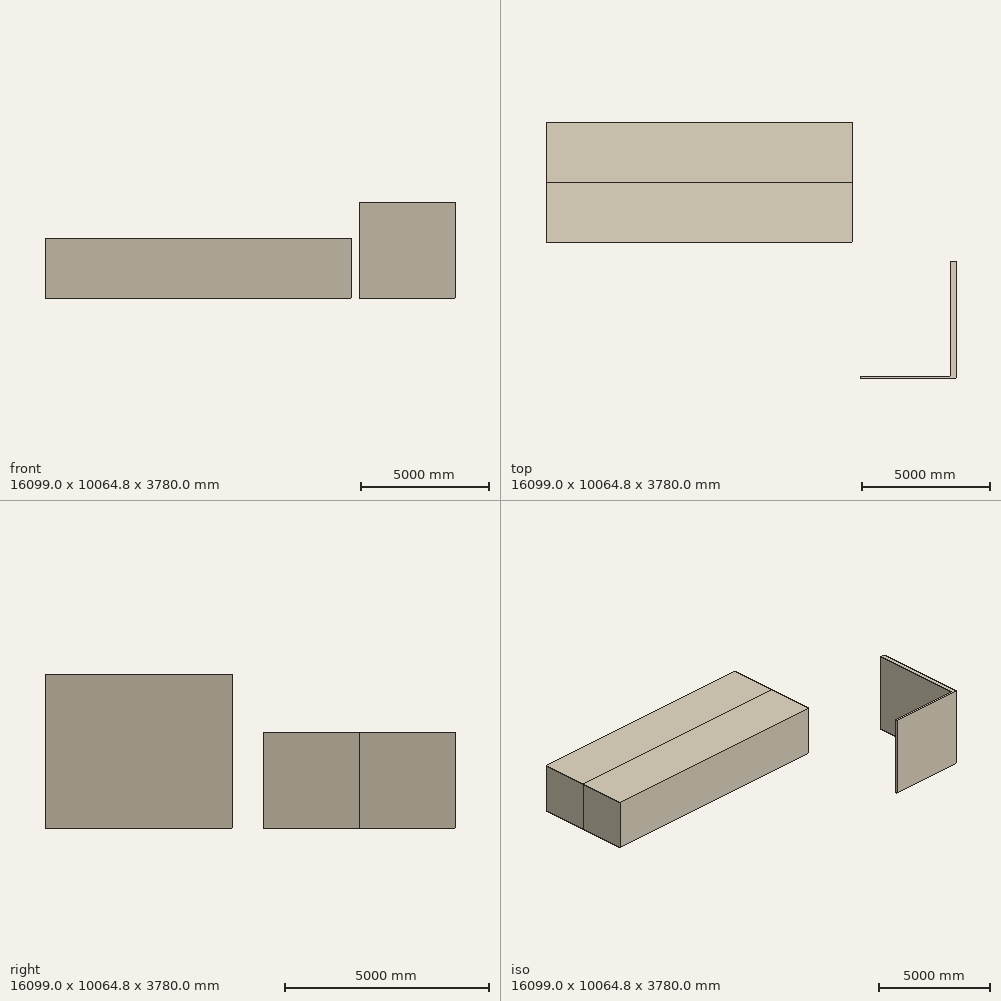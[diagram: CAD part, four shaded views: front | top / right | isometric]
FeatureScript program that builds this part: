
annotation { "Feature Type Name" : "Feature", "Feature Type Description" : "" }
export const myFeature = defineFeature(function(context is Context, id is Id, definition is map)
    precondition{}
    {
        {
            var Q0;
            Q0=qCreatedBy(makeId("Top.planeOp"),FACE);
            var sketch = newSketch(context, id + "F0", { "sketchPlane" : qUnion([Q0])});
            skLineSegment(sketch, "E0.bottom", {"start": v(0, 0) * mm, "end": v(12029, 0) * mm});
            skLineSegment(sketch, "E0.top", {"start": v(0, 2346) * mm, "end": v(12029, 2346) * mm});
            skLineSegment(sketch, "E0.left", {"start": v(0, 0) * mm, "end": v(0, 2346) * mm});
            skLineSegment(sketch, "E0.right", {"start": v(12029, 0) * mm, "end": v(12029, 2346) * mm});
            skLineSegment(sketch, "E1.bottom", {"start": v(0, 2356) * mm, "end": v(12029, 2356) * mm});
            skLineSegment(sketch, "E1.top", {"start": v(0, 4702) * mm, "end": v(12029, 4702) * mm});
            skLineSegment(sketch, "E1.left", {"start": v(0, 2356) * mm, "end": v(0, 4702) * mm});
            skLineSegment(sketch, "E1.right", {"start": v(12029, 2356) * mm, "end": v(12029, 4702) * mm});
            skSolve(sketch);
        }
        {
            var Q0;
            Q0=makeQuery(id+"F0.imprint","IMPRINT",FACE,{"disambiguationData":[TD([[makeQuery(id+"F0.imprint","IMPRINT",EDGE,{"derivedFrom":sQuery(id+"F0.wireOp",EDGE,"E0.bottom")}),1.0]])]});
            var Q1;
            Q1=makeQuery(id+"F0.imprint","IMPRINT",FACE,{"disambiguationData":[TD([[makeQuery(id+"F0.imprint","IMPRINT",EDGE,{"derivedFrom":sQuery(id+"F0.wireOp",EDGE,"E1.bottom")}),1.0]])]});
            extrude(context, id + "F1", {"entities" : qUnion([Q0, Q1]), "depth" : 2359 * mm, "offsetDistance" : 25 * mm});
        }
        {
            var Q0;
            Q0=qCreatedBy(makeId("Top.planeOp"),FACE);
            var sketch = newSketch(context, id + "F2", { "sketchPlane" : qUnion([Q0])});
            skLineSegment(sketch, "E2", {"start": v(12029, 4702) * mm, "end": v(15529, 4702) * mm});
            skLineSegment(sketch, "E3", {"start": v(15529, 4702) * mm, "end": v(15529, 4302) * mm});
            skLineSegment(sketch, "E4", {"start": v(15529, 4302) * mm, "end": v(15879, 4302) * mm});
            skLineSegment(sketch, "E5", {"start": v(15879, 4302) * mm, "end": v(15879, 1737.16) * mm});
            skLineSegment(sketch, "E6", {"start": v(15879, 1737.16) * mm, "end": v(16099, 1737.16) * mm});
            skLineSegment(sketch, "E7", {"start": v(16099, 1737.16) * mm, "end": v(16099, 4882.86) * mm});
            skLineSegment(sketch, "E8", {"start": v(16099, 4882.86) * mm, "end": v(12029, 4882.86) * mm});
            skLineSegment(sketch, "E9", {"start": v(12029, 4882.86) * mm, "end": v(12029, 4702) * mm});
            skLineSegment(sketch, "E10", {"start": v(15879, -762.84) * mm, "end": v(16099, -762.84) * mm});
            skLineSegment(sketch, "E11", {"start": v(16099, -762.84) * mm, "end": v(16099, -5362.84) * mm});
            skLineSegment(sketch, "E12", {"start": v(15879, -5262.84) * mm, "end": v(12329, -5262.84) * mm});
            skLineSegment(sketch, "E13", {"start": v(12429, -5283.95) * mm, "end": v(12429, -1250) * mm});
            skLineSegment(sketch, "E14", {"start": v(12429, -1250) * mm, "end": v(12029, -1250) * mm});
            skLineSegment(sketch, "E15", {"start": v(12029, -1250) * mm, "end": v(12029, 0) * mm});
            skLineSegment(sketch, "E16", {"start": v(12029, 0) * mm, "end": v(11929, 0) * mm});
            skLineSegment(sketch, "E17", {"start": v(11929, 0) * mm, "end": v(11929, -1350) * mm});
            skLineSegment(sketch, "E18", {"start": v(11929, -1350) * mm, "end": v(12329, -1350) * mm});
            skLineSegment(sketch, "E19", {"start": v(12329, -1350) * mm, "end": v(12329, -5362.84) * mm});
            skLineSegment(sketch, "E20", {"start": v(12329, -5362.84) * mm, "end": v(16099, -5362.84) * mm});
            skLineSegment(sketch, "E21", {"start": v(15879, -5262.84) * mm, "end": v(15879, -762.84) * mm});
            skSolve(sketch);
        }
        {
            var Q0;
            Q0=makeQuery(id+"F2.imprint","IMPRINT",FACE,{"disambiguationData":[TD([[makeQuery(id+"F2.imprint","IMPRINT",EDGE,{"derivedFrom":sQuery(id+"F2.wireOp",EDGE,"E10")}),-1.0]])]});
            extrude(context, id + "F3", {"entities" : qUnion([Q0]), "depth" : 3780 * mm, "offsetDistance" : 25 * mm});
        }
    });
